# Revit family: Doorset_Emergency Exit Door with Escape Control Alarm_ASSA ABLOY DE_Hardware Light
name_source: partatom
category: Doors
revit_build: Autodesk Revit 2015 (Build: 20140606_1530(x64)
units: mm (PartAtom-declared; Revit-internal decimal feet)

## types (7) — shared parameters
Architectural Hardware = 1x Handle (inside) + Knob (outside)_OneSystem_ASSA ABLOY
BIMobject Brand = ASSA ABLOY DE
BIMobject Instructions Video = https://www.youtube.com
BIMobject Product Family = Exterior Door Solutions
BIMobject Product Group = Singe-Steel/Aluminium-Self Closing-Panic Device-Escape Route
BIMobject Product Page = http://bimobject.com
BIMobject Unique ref = ES1-ML-PE-ET-DC-DE09
Date of publishing = 22.09.2016
Description = Self Closing Door with Escape route technology
Door Closers = 1x Door Closer DC700 with guide rail_Cam-Motion®_ASSA ABLOY
Edition number = 1
Frame Material = Steel/Aluminium
Function = Exterior
Hardware Set = ES1-ML-PE-ET-DC-DE09
IFC Classification = Door
Locksets = 1x Security Panic Lock_OneSystem_ASSA ABLOY
Manufacturer = ASSA ABLOY
Maximum Door Height = 3750 mm  [stored 12.3031 ft]
Maximum Door Width = 1500 mm  [stored 4.92126 ft]
Maximum Thickness = 105 mm  [stored 0.344488 ft]
Minimum Door Height = 2110 mm  [stored 6.92257 ft]
Minimum Door Width = 900 mm  [stored 2.95276 ft]
Minimum Thickness = 38 mm  [stored 0.124672 ft]
Model = Doorset_Emergency Exit Door w/ Escape Control Alarm_ASSA ABLOY DE_Hardware Light
NBS Reference Code = 59-23
NBS Reference Description = Doorsets
Name = Emergency Exit Door w/ Escape Control Alarm
OmniClass Number = 23-17 11 00
OmniClass Title = Doors
Panel Material = Steel/Aluminium
Panic and Exit Devices = 1x EXITalarm_7411-10_Effeff
Product Guid = c7f00f5c-4d04-4900-b7e4-f101e5518ac1
Provider = ASSA ABLOY DE
Thickness = 90 mm  [stored 0.295276 ft]
Thickness Constraint = 90 mm  [stored 0.295276 ft]
URL = http://www.assaabloy.de
Uniclass 1.4 Code = L411
Uniclass 1.4 Description = Doors
Uniclass 2.0 Code = PR-59-23
Uniclass 2.0 Description = Doorsets
Wall Closure = By host

## per-type parameters (varying)
| type | Frame Height | Frame Width | Height | Panel Height | Panel Width | Rough Height | Rough Width | Width |
| 900 x 2110 mm (1000 x 2160 mm) | 2160 mm  [stored 7.08661 ft] | 1000 mm  [stored 3.28084 ft] | 2160 mm  [stored 7.08661 ft] | 2110 mm  [stored 6.92257 ft] | 900 mm  [stored 2.95276 ft] | 2172 mm  [stored 7.12598 ft] | 1024 mm  [stored 3.35958 ft] | 1000 mm  [stored 3.28084 ft] |
| 1000 x 2110 mm (1100 x 2160 mm) | 2160 mm  [stored 7.08661 ft] | 1100 mm | 2160 mm  [stored 7.08661 ft] | 2110 mm  [stored 6.92257 ft] | 1000 mm  [stored 3.28084 ft] | 2172 mm  [stored 7.12598 ft] | 1124 mm  [stored 3.68766 ft] | 1100 mm |
| 1000 x 2500 mm (1100 x 2550 mm) | 2550 mm  [stored 8.36614 ft] | 1100 mm | 2550 mm  [stored 8.36614 ft] | 2500 mm  [stored 8.2021 ft] | 1000 mm  [stored 3.28084 ft] | 2562 mm  [stored 8.40551 ft] | 1124 mm  [stored 3.68766 ft] | 1100 mm |
| 1000 x 3750 mm (1100 x 3800 mm) | 3800 mm  [stored 12.4672 ft] | 1100 mm | 3800 mm  [stored 12.4672 ft] | 3750 mm  [stored 12.3031 ft] | 1000 mm  [stored 3.28084 ft] | 3812 mm  [stored 12.5066 ft] | 1124 mm  [stored 3.68766 ft] | 1100 mm |
| 1300 x 2500 mm (1400 x 2550 mm) | 2550 mm  [stored 8.36614 ft] | 1400 mm  [stored 4.59318 ft] | 2550 mm  [stored 8.36614 ft] | 2500 mm  [stored 8.2021 ft] | 1300 mm  [stored 4.26509 ft] | 2562 mm  [stored 8.40551 ft] | 1424 mm  [stored 4.67192 ft] | 1400 mm  [stored 4.59318 ft] |
| 1300 x 3750 mm (1400 x 3800 mm) | 3800 mm  [stored 12.4672 ft] | 1400 mm  [stored 4.59318 ft] | 3800 mm  [stored 12.4672 ft] | 3750 mm  [stored 12.3031 ft] | 1300 mm  [stored 4.26509 ft] | 3812 mm  [stored 12.5066 ft] | 1424 mm  [stored 4.67192 ft] | 1400 mm  [stored 4.59318 ft] |
| 1500 x 3750 mm (1600 x 3800 mm) | 3800 mm  [stored 12.4672 ft] | 1600 mm  [stored 5.24934 ft] | 3800 mm  [stored 12.4672 ft] | 3750 mm  [stored 12.3031 ft] | 1500 mm  [stored 4.92126 ft] | 3812 mm  [stored 12.5066 ft] | 1624 mm  [stored 5.32808 ft] | 1600 mm  [stored 5.24934 ft] |

note: column(s) folded — value = type name in every type: Type Comments

note: [stored X ft] marks values corroborated as IEEE doubles in the binary element streams (Revit-internal decimal feet)

## geometry (parser evidence)
native form markers: Blend x6, Sweep x1
no freeform markers — native parametric forms only
